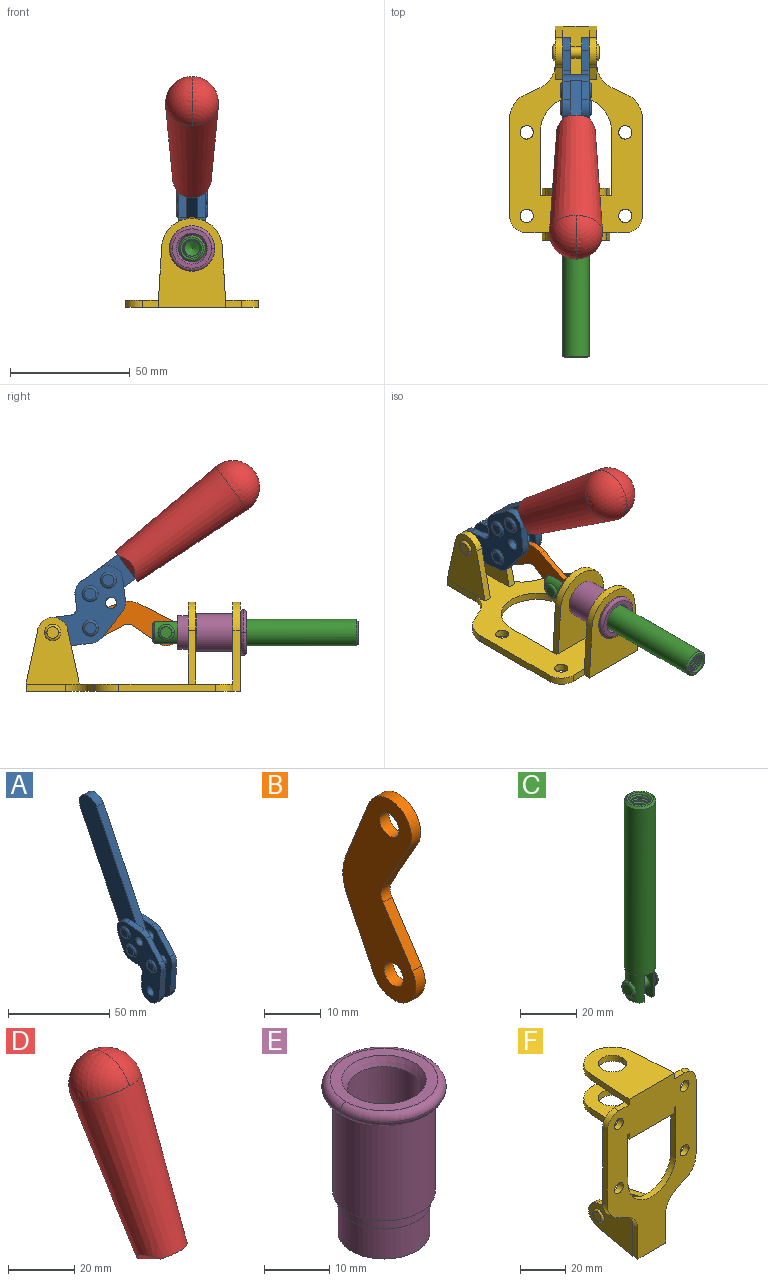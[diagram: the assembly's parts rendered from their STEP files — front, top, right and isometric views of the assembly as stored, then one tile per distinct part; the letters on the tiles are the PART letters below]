
ASSEMBLY  parts=6 mates=6
PART A: 59 faces, bbox 12.9x60.2x99.6 mm
  f0: torus R=2.39mm, axis (-1,0,0), area 14.9mm2, adj f20,f43,f51
  f1: torus R=2.39mm, axis (-1,0,0), area 14.9mm2, adj f19,f42,f51
  f2: torus R=2.39mm, axis (-1,0,0), area 14.9mm2, adj f18,f35,f51
  f3: torus R=2.39mm, axis (-1,0,0), area 14.9mm2, adj f14,f17,f23
  f4: torus R=2.39mm, axis (-1,0,0), area 14.9mm2, adj f13,f16,f23
  f5: torus R=2.39mm, axis (-1,0,0), area 14.9mm2, adj f12,f15,f23
  f6: cylinder r=2.39mm len=4.78mm, axis (1,0,0), area 46.5mm2, adj f48,f50,f51
  f7: cylinder r=2.39mm len=4.78mm, axis (1,0,0), area 46.5mm2, adj f50,f51
  f8: cylinder r=6.35mm len=12.68mm, axis (1,0,0), area 61.8mm2, adj f38,f39,f50,f51
  f9: cylinder r=2.39mm len=4.78mm, axis (-1,0,0), area 70.5mm2, adj f46,f50
  f10: cylinder r=2.39mm len=4.78mm, axis (-1,0,0), area 46.5mm2, adj f23,f45,f46
  f11: cylinder r=2.39mm len=4.78mm, axis (-1,0,0), area 46.5mm2, adj f23,f46
  f12: plane 4.78x4.78mm, normal (1,0,0), area 17.9mm2, adj f5,f15
  f13: plane 4.78x4.78mm, normal (1,0,0), area 17.9mm2, adj f4,f16
  f14: plane 4.78x4.78mm, normal (1,0,0), area 17.9mm2, adj f3,f17
  f15: torus R=2.39mm, axis (-1,0,0), area 14.9mm2, adj f5,f12,f23
  f16: torus R=2.39mm, axis (-1,0,0), area 14.9mm2, adj f4,f13,f23
  f17: torus R=2.39mm, axis (-1,0,0), area 14.9mm2, adj f3,f14,f23
  f18: plane 4.78x4.78mm, normal (-1,0,0), area 17.9mm2, adj f2,f35
  f19: plane 4.78x4.78mm, normal (-1,0,0), area 17.9mm2, adj f1,f42
  f20: plane 4.78x4.78mm, normal (-1,0,0), area 17.9mm2, adj f0,f43
  f21: plane 2.26x0.2mm, normal (1,0,0), area 0.2mm2, adj f31,f44
  f22: plane 2.26x0.2mm, normal (-1,0,0), area 0.2mm2, adj f41,f44
  f23: plane 39.37x30.77mm, normal (1,0,0), area 565.5mm2, adj f3,f4,f5,f10,f11,f15,f16,f17
  f24: cylinder r=6.1mm len=4.15mm, axis (-1,0,0), area 14.7mm2, adj f23,f25,f32,f46
  f25: plane 10.25x9.01mm, normal (0,-0.75,0.66), area 42.3mm2, adj f23,f24,f26,f46
  f26: cylinder r=6.35mm len=4.64mm, axis (-1,0,0), area 15.6mm2, adj f23,f25,f27,f46
  f27: plane 15.84x3.1mm, normal (0,-1,-0.07), area 49.2mm2, adj f23,f26,f28,f46
  f28: cylinder r=6.35mm len=12.68mm, axis (-1,0,0), area 61.8mm2, adj f23,f27,f29,f46
  f29: plane 8.11x3.1mm, normal (0,1,0.07), area 25.2mm2, adj f23,f28,f30,f46
  f30: cylinder r=3.05mm len=3.25mm, axis (-1,0,0), area 14.8mm2, adj f23,f29,f31,f46
  f31: plane 5.99x3.1mm, normal (0,0.07,-1), area 18.6mm2, adj f21,f23,f30,f44,f46
  f32: plane 9.5x3.1mm, normal (0,-0.07,1), area 29.5mm2, adj f23,f24,f33,f46,f47
  f33: cylinder r=6.1mm len=8.63mm, axis (-1,0,0), area 39.1mm2, adj f23,f32,f34,f47
  f34: plane 8.65x3.96mm, normal (0,0.91,-0.42), area 29.5mm2, adj f23,f33,f44,f47
  f35: torus R=2.39mm, axis (-1,0,0), area 14.9mm2, adj f2,f18,f51
  f36: plane 10.25x9.01mm, normal (0,-0.75,0.66), area 42.3mm2, adj f37,f49,f50,f51
  f37: cylinder r=6.35mm len=4.64mm, axis (1,0,0), area 15.6mm2, adj f36,f38,f50,f51
  f38: plane 15.84x3.1mm, normal (0,-1,-0.07), area 49.2mm2, adj f8,f37,f50,f51
  f39: plane 8.11x3.1mm, normal (0,1,0.07), area 25.2mm2, adj f8,f40,f50,f51
  f40: cylinder r=3.05mm len=3.25mm, axis (1,0,0), area 14.8mm2, adj f39,f41,f50,f51
  f41: plane 5.99x3.1mm, normal (0,0.07,-1), area 18.6mm2, adj f22,f40,f44,f50,f51
  f42: torus R=2.39mm, axis (-1,0,0), area 14.9mm2, adj f1,f19,f51
  f43: torus R=2.39mm, axis (-1,0,0), area 14.9mm2, adj f0,f20,f51
  f44: cylinder r=6.35mm len=12.12mm, axis (-1,0,0), area 128.9mm2, adj f21,f22,f23,f31,f34,f41,f46,f47
  f45: plane 2.65x1.35mm, normal (1,0,0), area 1mm2, adj f10,f55
  f46: plane 39.08x20.42mm, normal (-1,0,0), area 412.5mm2, adj f9,f10,f11,f24,f25,f26,f27,f28
  f47: plane 77.62x39.82mm, normal (1,0,0), area 850mm2, adj f32,f33,f34,f44,f53,f54,f55
  f48: plane 2.65x1.35mm, normal (-1,0,0), area 1mm2, adj f6,f55
  f49: cylinder r=6.1mm len=4.15mm, axis (1,0,0), area 14.7mm2, adj f36,f50,f51,f56
  f50: plane 39.08x20.42mm, normal (1,0,0), area 412.5mm2, adj f6,f7,f8,f9,f36,f37,f38,f39
  f51: plane 39.37x30.77mm, normal (-1,0,0), area 565.5mm2, adj f0,f1,f2,f6,f7,f8,f35,f36
  f52: plane 8.65x3.96mm, normal (0,0.91,-0.42), area 29.5mm2, adj f44,f51,f57,f58
  f53: plane 68.49x33.4mm, normal (0,0.9,-0.44), area 358.1mm2, adj f44,f47,f54,f58
  f54: cylinder r=6.35mm len=12.06mm, axis (1,0,0), area 93.7mm2, adj f47,f53,f55,f58
  f55: plane 68.49x33.4mm, normal (0,-0.9,0.44), area 358.1mm2, adj f44,f45,f46,f47,f48,f50,f54,f58
  f56: plane 9.5x3.1mm, normal (0,-0.07,1), area 29.5mm2, adj f49,f50,f51,f57,f58
  f57: cylinder r=6.1mm len=8.63mm, axis (1,0,0), area 39.1mm2, adj f51,f52,f56,f58
  f58: plane 77.62x39.82mm, normal (-1,0,0), area 850mm2, adj f44,f52,f53,f54,f55,f56,f57
PART B: 12 faces, bbox 2.3x18.2x42.8 mm
  f0: cylinder r=2.4mm len=4.8mm, axis (1,0,0), area 34.9mm2, adj f4,f11
  f1: cylinder r=10.41mm len=8.47mm, axis (1,0,0), area 20.2mm2, adj f4,f9,f10,f11
  f2: cylinder r=3.05mm len=3.16mm, axis (1,0,0), area 7.7mm2, adj f4,f6,f7,f11
  f3: cylinder r=2.4mm len=4.8mm, axis (1,0,0), area 34.9mm2, adj f4,f11
  f4: plane 42.81x18.23mm, normal (-1,0,0), area 414.1mm2, adj f0,f1,f2,f3,f5,f6,f7,f8
  f5: cylinder r=5.54mm len=10.67mm, axis (1,0,0), area 41.8mm2, adj f4,f6,f10,f11
  f6: plane 11.66x6.53mm, normal (0,-0.87,-0.49), area 30.9mm2, adj f2,f4,f5,f11
  f7: plane 11.17x7.33mm, normal (0,-0.84,0.55), area 30.9mm2, adj f2,f4,f8,f11
  f8: cylinder r=5.54mm len=10.51mm, axis (1,0,0), area 41.8mm2, adj f4,f7,f9,f11
  f9: plane 13.67x6.67mm, normal (0,0.9,-0.44), area 35.1mm2, adj f1,f4,f8,f11
  f10: plane 14.1x5.7mm, normal (0,0.93,0.37), area 35.1mm2, adj f1,f4,f5,f11
  f11: plane 42.81x18.23mm, normal (1,0,0), area 414.1mm2, adj f0,f1,f2,f3,f5,f6,f7,f8
PART C: 48 faces, bbox 12.6x11.1x86.1 mm
  f0: torus R=2.41mm, axis (-1,0,0), area 15mm2, adj f30,f32,f34
  f1: torus R=2.41mm, axis (-1,0,0), area 15mm2, adj f29,f31,f33
  f2: cylinder r=5.54mm len=72.39mm, axis (0,0,1), area 2518.5mm2, adj f3,f4,f42,f43
  f3: cone r=5.54mm half-angle=45deg, axis (0,0,1), area 7.6mm2, adj f2,f5,f41
  f4: cone r=5.54mm half-angle=45deg, axis (0,0,-1), area 34.9mm2, adj f2,f39
  f5: cylinder r=5.08mm len=11.48mm, axis (0,0,1), area 108.3mm2, adj f3,f7,f8,f41
  f6: cylinder r=2.41mm len=4.83mm, axis (-1,0,0), area 71.2mm2, adj f40,f41
  f7: cylinder r=2.41mm len=4.83mm, axis (-1,0,0), area 7.6mm2, adj f5,f34
  f8: cone r=5.08mm half-angle=45deg, axis (0,0,1), area 10.6mm2, adj f5,f37,f41
  f9: cone r=3.98mm half-angle=45deg, axis (0,0,1), area 17.6mm2, adj f27,f39,f45,f46,f47
  f10: cylinder r=2.41mm len=4.83mm, axis (-1,0,0), area 7.6mm2, adj f33,f38
  f11: cylinder r=3.2mm len=6.4mm, axis (0,0,1), area 78.4mm2, adj f12,f28,f44,f45,f47
  f12: cylinder r=3.2mm len=6.4mm, axis (0,0,1), area 10.5mm2, adj f11,f13,f45,f47
  f13: cylinder r=3.2mm len=6.4mm, axis (0,0,1), area 10.5mm2, adj f12,f14,f45,f47
  f14: cylinder r=3.2mm len=6.4mm, axis (0,0,1), area 10.5mm2, adj f13,f15,f45,f47
  f15: cylinder r=3.2mm len=6.4mm, axis (0,0,1), area 10.5mm2, adj f14,f16,f45,f47
  f16: cylinder r=3.2mm len=6.4mm, axis (0,0,1), area 10.5mm2, adj f15,f17,f45,f47
  f17: cylinder r=3.2mm len=6.4mm, axis (0,0,1), area 10.5mm2, adj f16,f18,f45,f47
  f18: cylinder r=3.2mm len=6.4mm, axis (0,0,1), area 10.5mm2, adj f17,f19,f45,f47
  f19: cylinder r=3.2mm len=6.4mm, axis (0,0,1), area 10.5mm2, adj f18,f20,f45,f47
  f20: cylinder r=3.2mm len=6.4mm, axis (0,0,1), area 10.5mm2, adj f19,f21,f45,f47
  f21: cylinder r=3.2mm len=6.4mm, axis (0,0,1), area 10.5mm2, adj f20,f22,f45,f47
  f22: cylinder r=3.2mm len=6.4mm, axis (0,0,1), area 10.5mm2, adj f21,f23,f45,f47
  f23: cylinder r=3.2mm len=6.4mm, axis (0,0,1), area 10.5mm2, adj f22,f24,f45,f47
  f24: cylinder r=3.2mm len=6.4mm, axis (0,0,1), area 10.5mm2, adj f23,f25,f45,f47
  f25: cylinder r=3.2mm len=6.4mm, axis (0,0,1), area 10.5mm2, adj f24,f26,f45,f47
  f26: cylinder r=3.2mm len=6.4mm, axis (0,0,1), area 10.5mm2, adj f25,f27,f45,f47
  f27: cylinder r=3.2mm len=6.4mm, axis (0,0,1), area 7.4mm2, adj f9,f26,f45,f47
  f28: cone r=3.2mm half-angle=60deg, axis (0,0,1), area 37.2mm2, adj f11
  f29: plane 4.83x4.83mm, normal (-1,0,0), area 18.3mm2, adj f1,f31
  f30: plane 4.83x4.83mm, normal (1,0,0), area 18.3mm2, adj f0,f32
  f31: torus R=2.41mm, axis (-1,0,0), area 15mm2, adj f1,f29,f33
  f32: torus R=2.41mm, axis (-1,0,0), area 15mm2, adj f0,f30,f34
  f33: plane 6.83x6.83mm, normal (1,0,0), area 18.3mm2, adj f1,f10,f31
  f34: plane 6.83x6.83mm, normal (-1,0,0), area 18.3mm2, adj f0,f7,f32
  f35: cone r=5.08mm half-angle=45deg, axis (0,0,1), area 10.6mm2, adj f36,f38,f40
  f36: plane 7.25x1.97mm, normal (0,0,-1), area 10mm2, adj f35,f40
  f37: plane 7.25x1.97mm, normal (0,0,-1), area 10mm2, adj f8,f41
  f38: cylinder r=5.08mm len=11.48mm, axis (0,0,1), area 108.3mm2, adj f10,f35,f40,f42
  f39: plane 9.55x9.55mm, normal (0,0,1), area 22mm2, adj f4,f9
  f40: plane 12.76x10.09mm, normal (1,0,0), area 95.7mm2, adj f6,f35,f36,f38,f42,f43
  f41: plane 12.76x10.09mm, normal (-1,0,0), area 95.7mm2, adj f3,f5,f6,f8,f37,f43
  f42: cone r=5.54mm half-angle=45deg, axis (0,0,1), area 7.6mm2, adj f2,f38,f40
  f43: plane 11.07x4.7mm, normal (0,0,-1), area 50.4mm2, adj f2,f40,f41
  f44: plane 0.89x0.62mm, normal (-1,0,0), area 0.3mm2, adj f11,f45,f46,f47
  f45: bspline ~24.8x7.63mm, area 266.6mm2, adj f9,f11,f12,f13,f14,f15,f16,f17
  f46: bspline ~24.87x7.63mm, area 73.6mm2, adj f9,f44,f45,f47
  f47: bspline ~24.98x7.63mm, area 272.5mm2, adj f9,f11,f12,f13,f14,f15,f16,f17
PART D: 11 faces, bbox 22.3x42.6x64.5 mm
  f0: sphere r=11.13mm, area 411.4mm2, adj f1,f8
  f1: cone r=11.11mm half-angle=3.3deg, axis (0,0.44,0.9), area 3251.8mm2, adj f0,f7,f8,f9,f10
  f2: cylinder r=6.16mm len=11.7mm, axis (1,0,0), area 89.5mm2, adj f3,f4,f5,f6
  f3: plane 60.23x36.75mm, normal (-1,0,0), area 763.6mm2, adj f2,f4,f6,f10
  f4: plane 51.37x25.05mm, normal (0,0.9,-0.44), area 264.2mm2, adj f2,f3,f5,f10
  f5: plane 60.23x36.75mm, normal (1,0,0), area 763.6mm2, adj f2,f4,f6,f10
  f6: plane 51.37x25.05mm, normal (0,-0.9,0.44), area 264.2mm2, adj f2,f3,f5,f10
  f7: plane 9.95x5.95mm, normal (0.71,-0.31,-0.64), area 25.8mm2, adj f1,f10
  f8: sphere r=11.13mm, area 411.4mm2, adj f0,f1
  f9: plane 9.95x5.95mm, normal (-0.71,-0.31,-0.64), area 25.8mm2, adj f1,f10
  f10: plane 14.27x11.38mm, normal (0,-0.44,-0.9), area 106.7mm2, adj f1,f3,f4,f5,f6,f7,f9
PART E: 15 faces, bbox 20.6x20.6x28.7 mm
  f0: torus R=8.26mm, axis (0,0,1), area 56.8mm2, adj f1,f10,f12
  f1: torus R=8.26mm, axis (0,0,1), area 56.8mm2, adj f0,f6,f13
  f2: cylinder r=5.59mm len=25.91mm, axis (0,0,1), area 909.6mm2, adj f3,f4
  f3: cone r=6.86mm half-angle=45deg, axis (0,0,-1), area 70.2mm2, adj f2,f14
  f4: cone r=6.47mm half-angle=30deg, axis (0,0,1), area 66.7mm2, adj f2,f13
  f5: cylinder r=7.04mm len=14.07mm, axis (0,0,1), area 252.6mm2, adj f11,f14
  f6: torus R=8.26mm, axis (0,0,1), area 56.8mm2, adj f1,f12,f13
  f7: cylinder r=7.16mm len=14.33mm, axis (0,0,1), area 91.5mm2, adj f9,f11
  f8: cylinder r=7.86mm len=18.42mm, axis (0,0,1), area 909.6mm2, adj f9,f10
  f9: plane 15.72x15.72mm, normal (0,0,-1), area 33mm2, adj f7,f8
  f10: plane 16.51x16.51mm, normal (0,0,-1), area 19.9mm2, adj f0,f8,f12
  f11: plane 14.33x14.33mm, normal (0,0,-1), area 5.7mm2, adj f5,f7
  f12: torus R=8.26mm, axis (0,0,1), area 56.8mm2, adj f0,f6,f10
  f13: plane 16.51x16.51mm, normal (0,0,1), area 82.7mm2, adj f1,f4,f6
  f14: plane 14.07x14.07mm, normal (0,0,-1), area 7.8mm2, adj f3,f5
PART F: 55 faces, bbox 55.7x37.4x89.8 mm
  f0: torus R=2.41mm, axis (-1,0,0), area 15mm2, adj f11,f15,f25
  f1: torus R=2.41mm, axis (-1,0,0), area 15mm2, adj f10,f12,f22
  f2: cylinder r=2.78mm len=5.56mm, axis (0,-1,0), area 54.2mm2, adj f30,f54
  f3: cylinder r=14.99mm len=29.97mm, axis (0,-1,0), area 145.9mm2, adj f30,f49,f53,f54
  f4: cylinder r=2.78mm len=5.56mm, axis (0,-1,0), area 54.2mm2, adj f30,f54
  f5: cylinder r=2.78mm len=5.56mm, axis (0,-1,0), area 54.2mm2, adj f30,f54
  f6: cylinder r=2.78mm len=5.56mm, axis (0,-1,0), area 54.2mm2, adj f30,f54
  f7: cylinder r=6.35mm len=12.7mm, axis (0,0,1), area 123.6mm2, adj f27,f51
  f8: cylinder r=6.35mm len=12.7mm, axis (0,0,-1), area 124.7mm2, adj f21,f35
  f9: cylinder r=2.41mm len=11.18mm, axis (-1,0,0), area 169.4mm2, adj f16,f19
  f10: plane 4.83x4.83mm, normal (1,0,0), area 18.3mm2, adj f1,f12
  f11: plane 4.83x4.83mm, normal (-1,0,0), area 18.3mm2, adj f0,f15
  f12: torus R=2.41mm, axis (-1,0,0), area 15mm2, adj f1,f10,f22
  f13: cylinder r=6.35mm len=12.41mm, axis (1,0,0), area 53.4mm2, adj f18,f19,f22,f23
  f14: cylinder r=6.35mm len=12.41mm, axis (-1,0,0), area 53.4mm2, adj f16,f17,f24,f25
  f15: torus R=2.41mm, axis (-1,0,0), area 15mm2, adj f0,f11,f25
  f16: plane 27.86x22.35mm, normal (1,0,0), area 425.4mm2, adj f9,f14,f17,f24,f30
  f17: plane 22.86x4.97mm, normal (0,0.21,0.98), area 72.5mm2, adj f14,f16,f25,f30
  f18: plane 22.86x4.97mm, normal (0,0.21,0.98), area 72.5mm2, adj f13,f19,f22,f30
  f19: plane 27.86x22.35mm, normal (-1,0,0), area 425.4mm2, adj f9,f13,f18,f23,f30
  f20: cylinder r=12.7mm len=25.35mm, axis (0,0,-1), area 119.8mm2, adj f21,f34,f35,f36
  f21: plane 34.21x28.07mm, normal (0,0,-1), area 702.4mm2, adj f8,f20,f30,f34,f36
  f22: plane 27.96x22.45mm, normal (1,0,0), area 407.2mm2, adj f1,f12,f13,f18,f23,f30,f42,f43
  f23: plane 22.86x4.97mm, normal (0,0.21,-0.98), area 72.5mm2, adj f13,f19,f22,f44
  f24: plane 22.86x4.97mm, normal (0,0.21,-0.98), area 72.5mm2, adj f14,f16,f25,f44
  f25: plane 27.86x22.35mm, normal (-1,0,0), area 407.1mm2, adj f0,f14,f15,f17,f24,f30,f45,f46
  f26: plane 3.1x0.95mm, normal (0,0,-1), area 2.7mm2, adj f30,f49,f50,f54
  f27: plane 34.21x28.07mm, normal (0,0,1), area 702.4mm2, adj f7,f28,f30,f50,f52
  f28: cylinder r=12.7mm len=25.35mm, axis (0,0,1), area 118.8mm2, adj f27,f50,f51,f52
  f29: plane 3.1x0.95mm, normal (0,0,-1), area 2.7mm2, adj f30,f52,f53,f54
  f30: plane 86.54x55.63mm, normal (0,1,0), area 2362.9mm2, adj f2,f3,f4,f5,f6,f16,f17,f18
  f31: plane 40.56x3.1mm, normal (-1,0,0), area 125.7mm2, adj f30,f32,f48,f54
  f32: cylinder r=7.11mm len=7.11mm, axis (0,-1,0), area 34.6mm2, adj f30,f31,f33,f54
  f33: plane 6.67x3.1mm, normal (0,0,1), area 20.4mm2, adj f30,f32,f34,f54
  f34: plane 25.39x3.13mm, normal (-1,0.06,0), area 79.5mm2, adj f20,f21,f33,f35,f54
  f35: plane 37.31x28.45mm, normal (0,0,1), area 789.9mm2, adj f8,f20,f34,f36,f54
  f36: plane 25.39x3.13mm, normal (1,0.06,0), area 79.5mm2, adj f20,f21,f35,f37,f54
  f37: plane 6.67x3.1mm, normal (0,0,1), area 20.4mm2, adj f30,f36,f38,f54
  f38: cylinder r=7.11mm len=7.11mm, axis (0,-1,0), area 34.6mm2, adj f30,f37,f39,f54
  f39: plane 40.56x3.1mm, normal (1,0,0), area 125.7mm2, adj f30,f38,f40,f54
  f40: cylinder r=11.18mm len=10.16mm, axis (0,-1,0), area 39.5mm2, adj f30,f39,f41,f54
  f41: plane 6.09x3.1mm, normal (0.42,0,-0.91), area 20.8mm2, adj f30,f40,f42,f54
  f42: cylinder r=11.18mm len=9.41mm, axis (0,-1,0), area 37.2mm2, adj f22,f30,f41,f43,f54
  f43: plane 16.5x3.1mm, normal (1,0,0), area 51.1mm2, adj f22,f42,f44,f54
  f44: plane 17.37x3.1mm, normal (0,0,-1), area 53.8mm2, adj f23,f24,f30,f43,f45,f54
  f45: plane 16.5x3.1mm, normal (-1,0,0), area 51.1mm2, adj f25,f44,f46,f54
  f46: cylinder r=11.18mm len=9.41mm, axis (0,-1,0), area 37.2mm2, adj f25,f30,f45,f47,f54
  f47: plane 6.09x3.1mm, normal (-0.42,0,-0.91), area 20.8mm2, adj f30,f46,f48,f54
  f48: cylinder r=11.18mm len=10.16mm, axis (0,-1,0), area 39.5mm2, adj f30,f31,f47,f54
  f49: plane 26.54x3.1mm, normal (-1,0,0), area 82.3mm2, adj f3,f26,f30,f54
  f50: plane 25.39x3.1mm, normal (1,0.06,0), area 78.8mm2, adj f26,f27,f28,f51,f54
  f51: plane 37.31x28.45mm, normal (0,0,-1), area 789.9mm2, adj f7,f28,f50,f52,f54
  f52: plane 25.39x3.1mm, normal (-1,0.06,0), area 78.8mm2, adj f27,f28,f29,f51,f54
  f53: plane 26.54x3.1mm, normal (1,0,0), area 82.3mm2, adj f3,f29,f30,f54
  f54: plane 89.66x55.63mm, normal (0,-1,0), area 2678.5mm2, adj f2,f3,f4,f5,f6,f26,f29,f31
PLACE A rot(axis=(1,0,0),79.3deg) t=(0,5.4,6.42)mm
PLACE B rot(axis=(1,0,0),95.4deg) t=(0,11.77,1.56)mm
PLACE C rot(axis=(1,0,0),90deg) t=(0,9.54,0)mm
PLACE D rot(axis=(1,0,0),79.3deg) t=(0,5.4,6.42)mm
PLACE E rot(axis=(1,0,0),90deg) t=(0,9.43,0)mm
PLACE F rot(axis=(1,0,0),90deg) t=(0,9.43,0)mm fixed
MATE revolute F.f0 <-> A.f7  axis (-1,0,0) through (0,41.52,24.61)mm
MATE slider C.f2 <-> E.f2  axis (0,-1,0) through (0,-49.24,24.61)mm
MATE revolute C.f6 <-> B.f5  axis (-1,0,0) through (0,-5.94,24.61)mm
MATE fastened A.f54 <-> D.f2  axis (1,0,0) through (0,-35.16,86.42)mm
MATE fastened E.f0 <-> F.f7  axis (0,1,0) through (0,-36.96,24.61)mm
MATE revolute A.f4 <-> B.f3  axis (-1,0,0) through (0,25.76,26.48)mm
